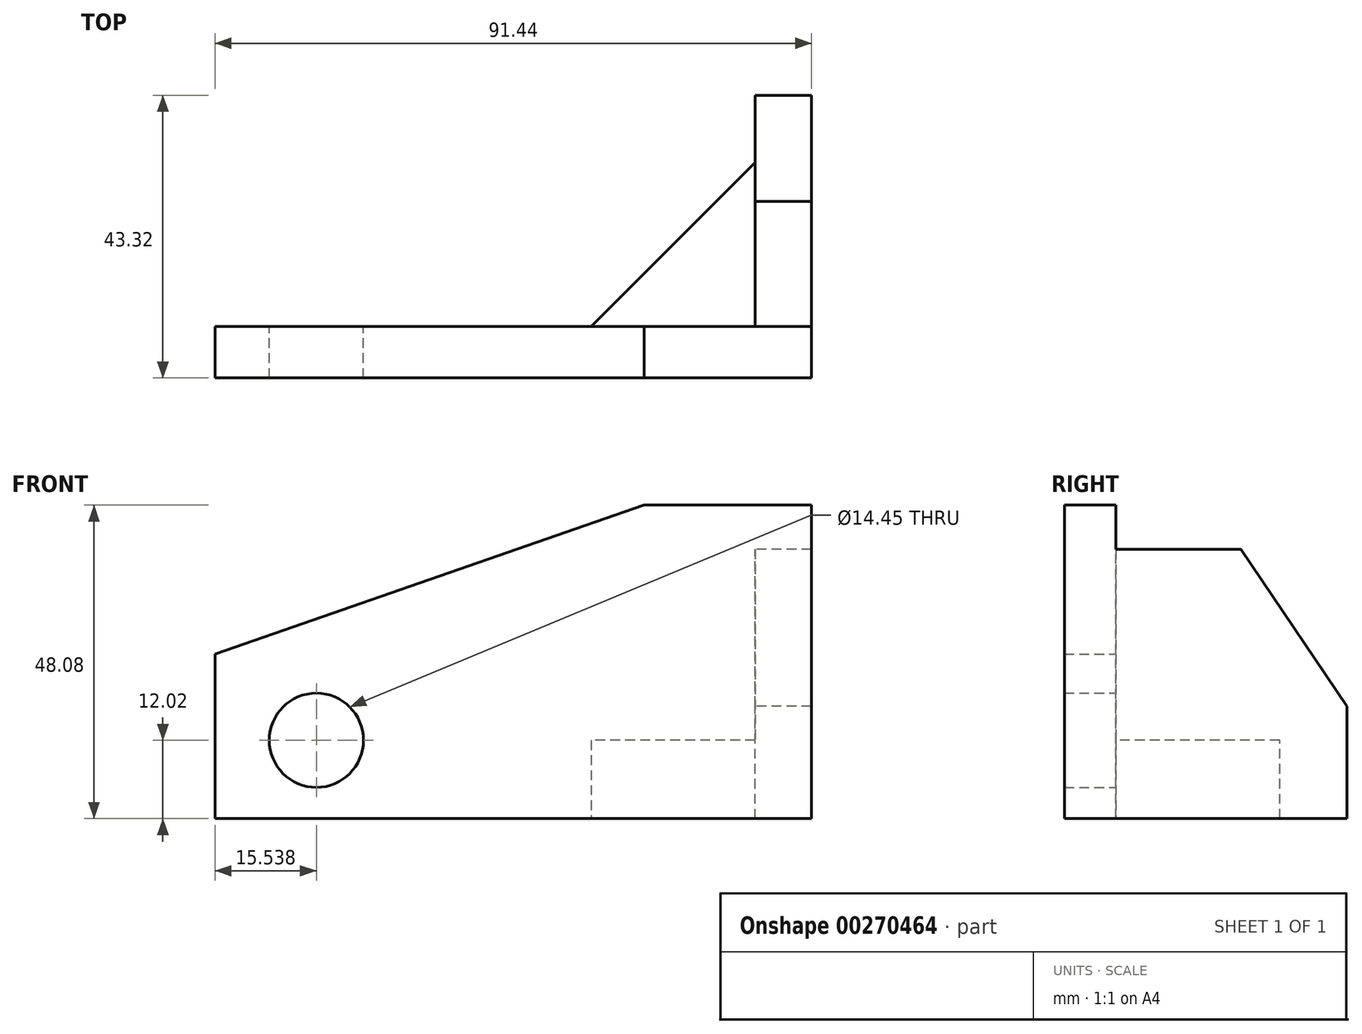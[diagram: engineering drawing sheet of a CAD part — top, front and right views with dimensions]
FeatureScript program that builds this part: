
annotation { "Feature Type Name" : "Feature", "Feature Type Description" : "" }
export const myFeature = defineFeature(function(context is Context, id is Id, definition is map)
    precondition{}
    {
        {
            var Q0;
            Q0=qCreatedBy(makeId("Right.planeOp"),FACE);
            var sketch = newSketch(context, id + "F0", { "sketchPlane" : qUnion([Q0])});
            skLineSegment(sketch, "E0.bottom", {"start": v(0, 29.26) * mm, "end": v(19.18, 29.26) * mm});
            skLineSegment(sketch, "E0.top", {"start": v(0, -12.02) * mm, "end": v(19.18, -12.02) * mm});
            skLineSegment(sketch, "E0.left", {"start": v(0, 29.26) * mm, "end": v(0, -12.02) * mm});
            skLineSegment(sketch, "E0.right", {"start": v(19.18, 29.26) * mm, "end": v(19.18, -12.02) * mm});
            skLineSegment(sketch, "E1", {"start": v(19.18, -12.02) * mm, "end": v(35.45, -12.02) * mm});
            skLineSegment(sketch, "E2", {"start": v(35.45, -12.02) * mm, "end": v(35.45, 5.22) * mm});
            skLineSegment(sketch, "E3", {"start": v(35.45, 5.22) * mm, "end": v(19.18, 29.26) * mm});
            skSolve(sketch);
        }
        {
            var Q0;
            Q0 = qSketchRegion(id + "F0", true);
            extrude(context, id + "F1", {"entities" : qUnion([Q0]), "depth" : 8.64 * mm});
        }
        {
            var Q0;
            Q0=makeQuery(id+"F1.opExtrude","SWEPT_FACE",FACE,{"disambiguationData":[OSD([sQuery(id+"F0.wireOp",EDGE,"E0.left")])]});
            var sketch = newSketch(context, id + "F2", { "sketchPlane" : qUnion([Q0])});
            skLineSegment(sketch, "E4.bottom", {"start": v(8.64, -12.02) * mm, "end": v(-17, -12.02) * mm});
            skLineSegment(sketch, "E4.top", {"start": v(8.64, 36.06) * mm, "end": v(-17, 36.06) * mm});
            skLineSegment(sketch, "E4.left", {"start": v(8.64, -12.02) * mm, "end": v(8.64, 36.06) * mm});
            skLineSegment(sketch, "E4.right", {"start": v(-17, -12.02) * mm, "end": v(-17, 36.06) * mm});
            skLineSegment(sketch, "E5.bottom", {"start": v(-17, -12.02) * mm, "end": v(-82.8, -12.02) * mm});
            skLineSegment(sketch, "E5.top", {"start": v(-17, 13.23) * mm, "end": v(-82.8, 13.23) * mm});
            skLineSegment(sketch, "E5.left", {"start": v(-17, -12.02) * mm, "end": v(-17, 13.23) * mm});
            skLineSegment(sketch, "E5.right", {"start": v(-82.8, -12.02) * mm, "end": v(-82.8, 13.23) * mm});
            skLineSegment(sketch, "E6", {"start": v(-82.8, 13.23) * mm, "end": v(-17, 36.06) * mm});
            skCircle(sketch, "E7", {"center": v(-67.26, 0) * mm, "radius": 7.22 * mm});
            skSolve(sketch);
        }
        {
            var Q0;
            Q0 = qSketchRegion(id + "F2", true);
            extrude(context, id + "F3", {"entities" : qUnion([Q0]), "operationType" : NewBodyOperationType.ADD, "depth" : 7.87 * mm});
        }
        {
            var Q0;
            Q0=makeQuery(id+"F3.opExtrude","CAP_FACE",FACE,{"disambiguationData":[OSD([sQuery(id+"F2.wireOp",EDGE,"E4.bottom"),sQuery(id+"F2.wireOp",EDGE,"E4.top"),sQuery(id+"F2.wireOp",EDGE,"E4.left"),sQuery(id+"F2.wireOp",EDGE,"E5.bottom"),sQuery(id+"F2.wireOp",EDGE,"E5.right"),sQuery(id+"F2.wireOp",EDGE,"E6"),sQuery(id+"F2.wireOp",EDGE,"E7")])],"isStart":true});
            var sketch = newSketch(context, id + "F4", { "sketchPlane" : qUnion([Q0])});
            skLineSegment(sketch, "E8.bottom", {"start": v(0, -12.02) * mm, "end": v(40.39, -12.02) * mm});
            skLineSegment(sketch, "E8.top", {"start": v(0, 0) * mm, "end": v(40.39, 0) * mm});
            skLineSegment(sketch, "E8.left", {"start": v(0, -12.02) * mm, "end": v(0, 0) * mm});
            skLineSegment(sketch, "E8.right", {"start": v(40.39, -12.02) * mm, "end": v(40.39, 0) * mm});
            skSolve(sketch);
        }
        {
            var Q0;
            Q0 = qSketchRegion(id + "F4", true);
            extrude(context, id + "F5", {"entities" : qUnion([Q0]), "operationType" : NewBodyOperationType.ADD, "depth" : 25.4 * mm});
        }
        {
            var Q0;
            Q0=makeQuery(id+"F5.opExtrude","CAP_EDGE",EDGE,{"disambiguationData":[OSD([sQuery(id+"F4.wireOp",EDGE,"E8.right")])],"isStart":false});
            chamfer(context, id + "F6", {"entities" : qUnion([Q0]), "width" : 40.64 * mm, "tangentPropagation" : true});
        }
    });
